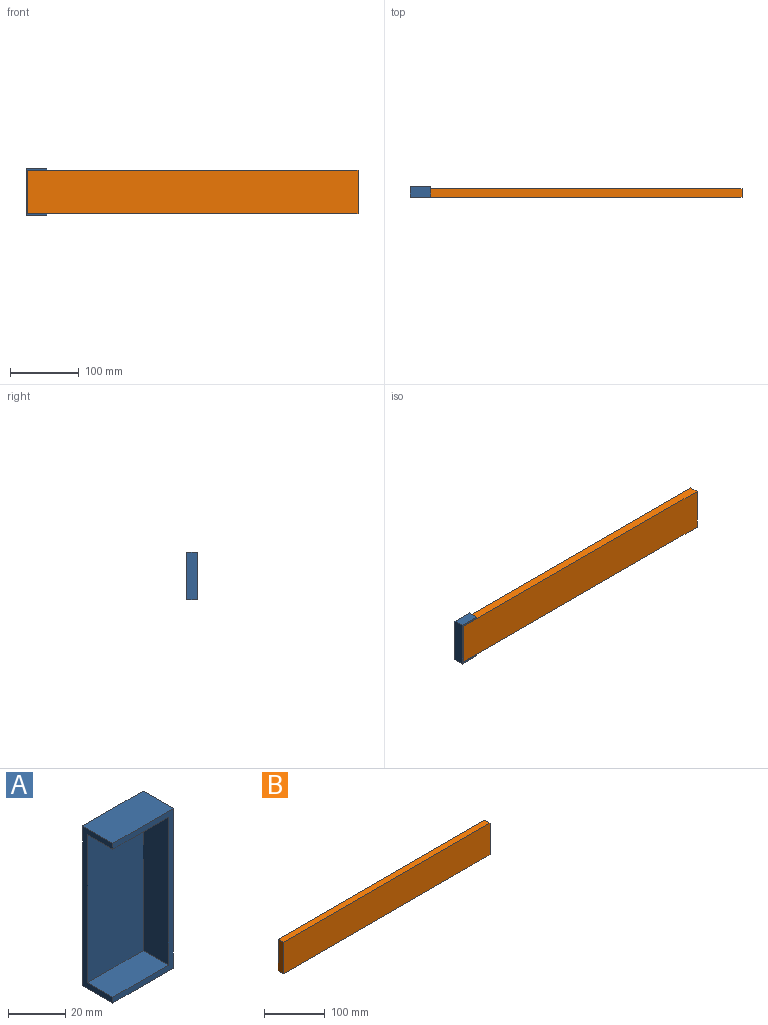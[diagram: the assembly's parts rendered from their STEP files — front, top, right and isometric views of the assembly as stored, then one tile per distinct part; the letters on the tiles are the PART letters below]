
ASSEMBLY  parts=2 mates=1
PART A: 10 faces, bbox 30x15x68.5 mm
  f0: plane 68.5x15mm, normal (-1,0,0), area 233.7mm2, adj f1,f2,f3,f5,f6,f7,f9
  f1: plane 30x15mm, normal (0,0,-1), area 450mm2, adj f0,f2,f4,f9
  f2: plane 68.5x30mm, normal (0,1,0), area 2055mm2, adj f0,f1,f3,f4
  f3: plane 30x15mm, normal (0,0,1), area 450mm2, adj f0,f2,f4,f9
  f4: plane 68.5x15mm, normal (1,0,0), area 1027.5mm2, adj f1,f2,f3,f9
  f5: plane 27.5x12.5mm, normal (0,0,1), area 343.8mm2, adj f0,f6,f8,f9
  f6: plane 63.5x27.5mm, normal (0,-1,0), area 1746.2mm2, adj f0,f5,f7,f8
  f7: plane 27.5x12.5mm, normal (0,0,-1), area 343.8mm2, adj f0,f6,f8,f9
  f8: plane 63.5x12.5mm, normal (-1,0,0), area 793.8mm2, adj f5,f6,f7,f9
  f9: plane 68.5x30mm, normal (0,-1,0), area 308.8mm2, adj f0,f1,f3,f4,f5,f7,f8
PART B: 6 faces, bbox 480x12.5x63.5 mm
  f0: plane 480x63.5mm, normal (0,-1,0), area 30480mm2, adj f1,f3,f4,f5
  f1: plane 480x12.5mm, normal (0,0,-1), area 6000mm2, adj f0,f2,f4,f5
  f2: plane 480x63.5mm, normal (0,1,0), area 30480mm2, adj f1,f3,f4,f5
  f3: plane 480x12.5mm, normal (0,0,1), area 6000mm2, adj f0,f2,f4,f5
  f4: plane 63.5x12.5mm, normal (1,0,0), area 793.8mm2, adj f0,f1,f2,f3
  f5: plane 63.5x12.5mm, normal (-1,0,0), area 793.8mm2, adj f0,f1,f2,f3
PLACE A rot(axis=(0,1,0),180deg) t=(67.5,0,0)mm
PLACE B t=(40,0,0)mm
MATE fastened A.f8 <-> B.f5  axis (1,0,0) through (40,0,0)mm
